# Revit family: Банкетка чугунная «Львы»
name_source: partatom
category: Антураж
revit_build: Autodesk Revit 2017 (Build: 20160225_1515(x64)
units: mm (PartAtom-declared; Revit-internal decimal feet)

## family parameters
Всегда вертикально = Да
Источник визуального образа = Геометрия семейства
На основе рабочей плоскости = Нет
Общий = Нет
При загрузке вырезать с полостями = Нет
Точка расчета площади = Нет

## types (5) — shared parameters
ADSK_Код изделия = 7209
ADSK_Материал доски = Лиственница
ADSK_Материал опоры = Чугун, серый
ADSK_Материал фурнитуры = Чугун, серый
ADSK_Наименование = Банкетка чугунная «Львы»
ADSK_Размер_Высота = 550 мм
ADSK_Размер_Ширина = 600 мм
URL = https://hobbyka.ru
Изготовитель = ООО "Хоббика"
Перемычка = Да
zero-valued in all types: Высота

## per-type parameters (varying)
| type | ADSK_Размер_Длина | Длина доски | Стоимость | Центральная опора |
| Банкетка чугунная «Львы» 1,5м | 1500 мм | 1683 мм | 18616 $ | Нет |
| Банкетка чугунная «Львы» 1,8м | 1800 мм | 1983 мм | 19440 $ | Нет |
| Банкетка чугунная «Львы» 2,0м (2 опоры) | 2000 мм | 2183 мм | 20016 $ | Нет |
| Банкетка чугунная «Львы» 2,0м (3 опоры) | 2000 мм | 2183 мм | 28038 $ | Да |
| Банкетка чугунная «Львы» 3,0м | 3000 мм | 3183 мм | 29961 $ | Да |
